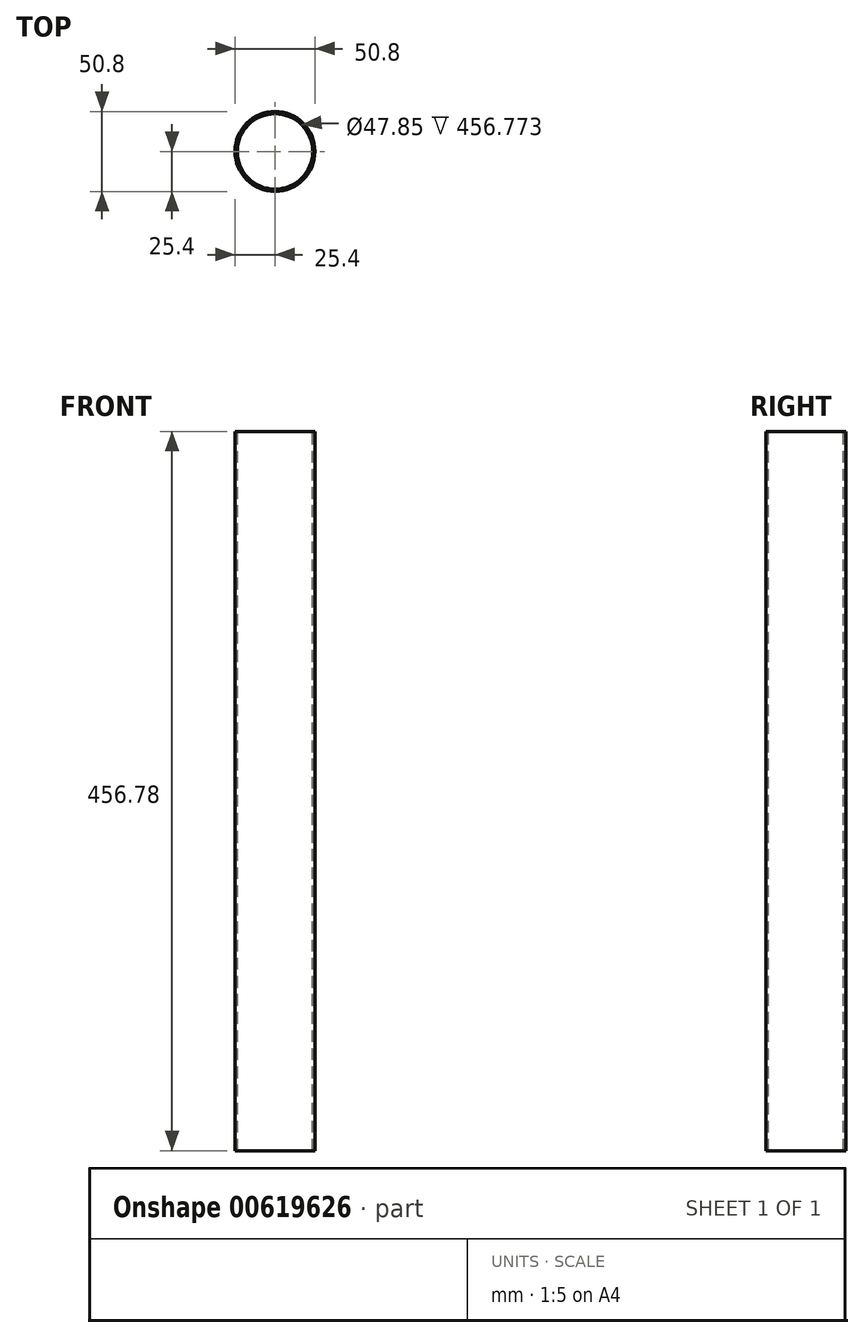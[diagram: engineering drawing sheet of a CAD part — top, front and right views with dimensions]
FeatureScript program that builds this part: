
annotation { "Feature Type Name" : "Feature", "Feature Type Description" : "" }
export const myFeature = defineFeature(function(context is Context, id is Id, definition is map)
    precondition{}
    {
        {
            var Q0;
            Q0=qCreatedBy(makeId("Front.planeOp"),FACE);
            var sketch = newSketch(context, id + "F0", { "sketchPlane" : qUnion([Q0])});
            skLineSegment(sketch, "E0.bottom", {"start": v(25.4, 228.39) * mm, "end": v(-25.4, 228.39) * mm});
            skLineSegment(sketch, "E0.top", {"start": v(25.4, -228.39) * mm, "end": v(-25.4, -228.39) * mm});
            skLineSegment(sketch, "E0.left", {"start": v(25.4, 228.39) * mm, "end": v(25.4, -228.39) * mm});
            skLineSegment(sketch, "E0.right", {"start": v(-25.4, 228.39) * mm, "end": v(-25.4, -228.39) * mm});
            skPoint(sketch, "E0.middle", {"position": v(0, 0) * mm});
            skLineSegment(sketch, "E1", {"start": v(0, 0) * mm, "end": v(0, -228.39) * mm});
            skLineSegment(sketch, "E2", {"start": v(0, 0) * mm, "end": v(0, 228.39) * mm});
            skSolve(sketch);
        }
        {
            var Q0;
            {var subQ0=sQuery(id+"F0.wireOp",EDGE,"E0.right");Q0=makeQuery(id+"F0.imprint","IMPRINT",FACE,{"disambiguationData":[TD([[makeQuery(id+"F0.imprint","IMPRINT",EDGE,{"derivedFrom":subQ0}),1.0]])]});}
            var Q1;
            Q1=sQuery(id+"F0.wireOp",EDGE,"E1");
            revolve(context, id + "F1", {"entities" : qUnion([Q0]), "axis" : qUnion([Q1]), "revolveType" : RevolveType.FULL});
        }
        {
            var Q0;
            Q0=makeQuery(id+"F1.opRevolve","SWEPT_FACE",FACE,{"disambiguationData":[OSD([sQuery(id+"F0.wireOp",EDGE,"E0.bottom")])]});
            var sketch = newSketch(context, id + "F2", { "sketchPlane" : qUnion([Q0])});
            skPoint(sketch, "E3", {"position": v(0, 0) * mm});
            skSolve(sketch);
        }
        {
            var Q0;
            Q0=sQuery(id+"F2.wireOp",VERTEX,"E3");
            var Q1;
            Q1=makeQuery(id+"F1.opRevolve","SWEPT_BODY",BODY,{"disambiguationData":[OSD([sQuery(id+"F0.wireOp",EDGE,"E0.bottom"),sQuery(id+"F0.wireOp",EDGE,"E0.top"),sQuery(id+"F0.wireOp",EDGE,"E0.right"),sQuery(id+"F0.wireOp",EDGE,"E1"),sQuery(id+"F0.wireOp",EDGE,"E2")])]});
            hole(context, id + "F3", {"style" : HoleStyle.SIMPLE, "endStyle" : HoleEndStyle.THROUGH, "holeDiameter" : 47.85 * mm, "majorDiameter" : 6.35 * mm, "isTappedThrough" : true, "tappedDepth" : 12.7 * mm, "tapClearance" : 3, "locations" : qUnion([Q0]), "scope" : qUnion([Q1])});
        }
    });
